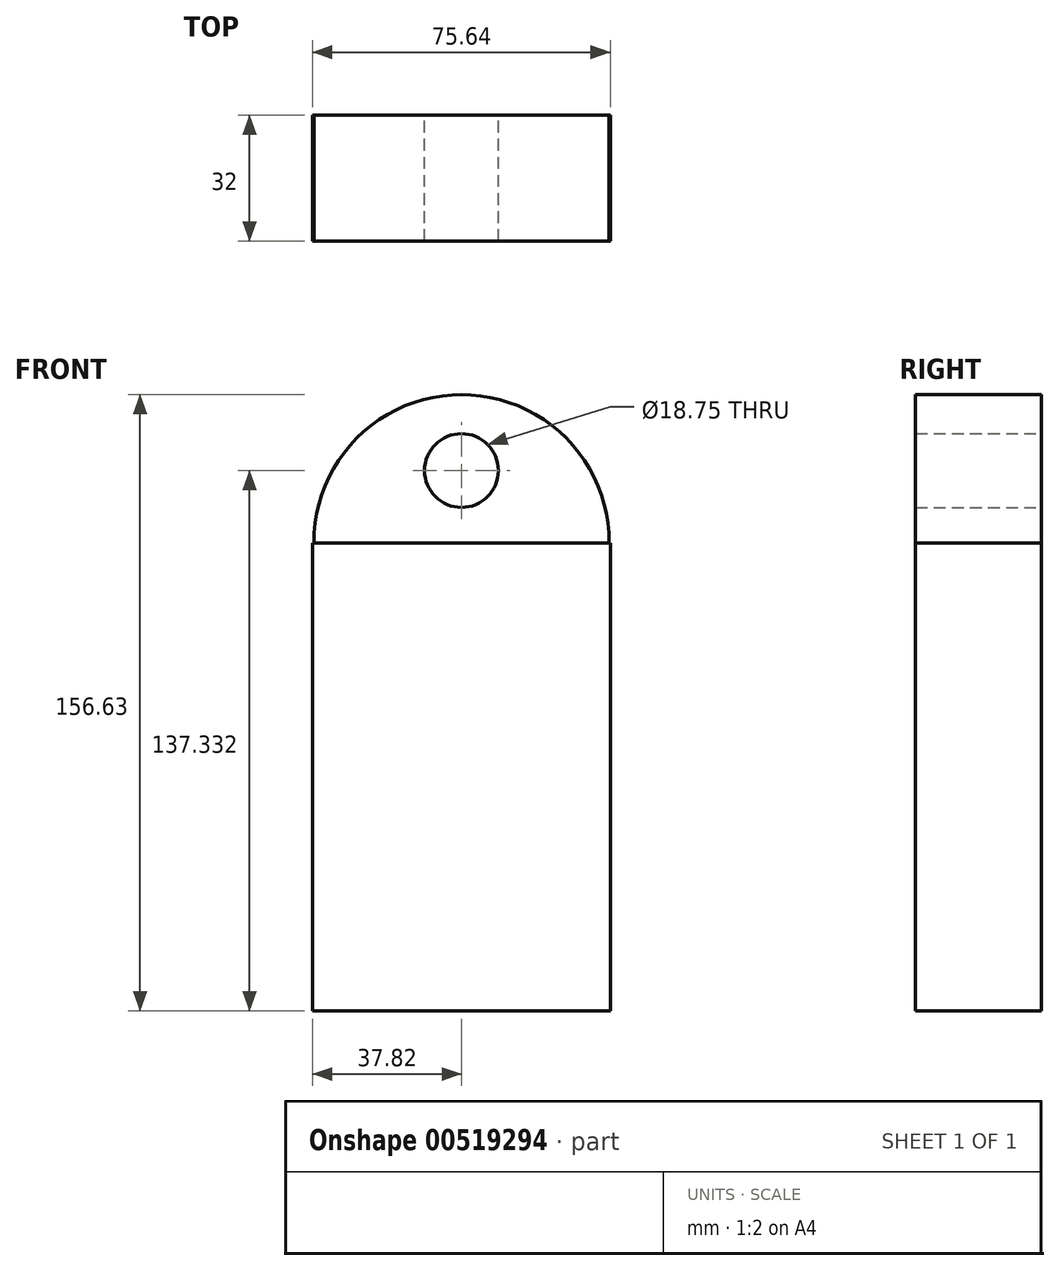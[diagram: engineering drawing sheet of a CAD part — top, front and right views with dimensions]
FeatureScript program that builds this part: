
annotation { "Feature Type Name" : "Feature", "Feature Type Description" : "" }
export const myFeature = defineFeature(function(context is Context, id is Id, definition is map)
    precondition{}
    {
        {
            var Q0;
            Q0=qCreatedBy(makeId("Front.planeOp"),FACE);
            var sketch = newSketch(context, id + "F0", { "sketchPlane" : qUnion([Q0])});
            skLineSegment(sketch, "E0.bottom", {"start": v(-37.82, 59.48) * mm, "end": v(37.82, 59.48) * mm});
            skLineSegment(sketch, "E0.top", {"start": v(-37.82, -59.48) * mm, "end": v(37.82, -59.48) * mm});
            skLineSegment(sketch, "E0.left", {"start": v(-37.82, 59.48) * mm, "end": v(-37.82, -59.48) * mm});
            skLineSegment(sketch, "E0.right", {"start": v(37.82, 59.48) * mm, "end": v(37.82, -59.48) * mm});
            skPoint(sketch, "E0.middle", {"position": v(0, 0) * mm});
            skSolve(sketch);
        }
        {
            var Q0;
            Q0=makeQuery(id+"F0.imprint","IMPRINT",FACE,{"disambiguationData":[TD([[makeQuery(id+"F0.imprint","IMPRINT",EDGE,{"derivedFrom":sQuery(id+"F0.wireOp",EDGE,"E0.bottom")}),-1.0]])]});
            var sketch = newSketch(context, id + "F1", { "sketchPlane" : qUnion([Q0])});
            skCircle(sketch, "E1", {"center": v(0, 59.66) * mm, "radius": 37.49 * mm});
            skSolve(sketch);
        }
        {
            var Q0;
            {var subQ0=sQuery(id+"F1.wireOp",EDGE,"E1");var subQ1=makeQuery(id+"F0.imprint","IMPRINT",EDGE,{"derivedFrom":sQuery(id+"F0.wireOp",EDGE,"E0.bottom")});var subQ2=makeQuery(id+"F1.imprint","INTERSECT",VERTEX,{"disambiguationData":[OD(0.0)],"derivedFrom":[subQ1,subQ0]});Q0=makeQuery(id+"F1.imprint","IMPRINT",FACE,{"disambiguationData":[TD([[makeQuery(id+"F1.imprint","IMPRINT",EDGE,{"disambiguationData":[TD([[subQ2,-1.0]])],"derivedFrom":subQ0}),1.0]])]});}
            var Q1;
            {var subQ0=sQuery(id+"F1.wireOp",EDGE,"E1");var subQ1=makeQuery(id+"F0.imprint","IMPRINT",EDGE,{"derivedFrom":sQuery(id+"F0.wireOp",EDGE,"E0.bottom")});var subQ2=makeQuery(id+"F1.imprint","INTERSECT",VERTEX,{"disambiguationData":[OD(0.0)],"derivedFrom":[subQ1,subQ0]});Q1=makeQuery(id+"F1.imprint","IMPRINT",FACE,{"disambiguationData":[TD([[makeQuery(id+"F1.imprint","IMPRINT",EDGE,{"disambiguationData":[TD([[subQ2,1.0]])],"derivedFrom":subQ0}),1.0]])]});}
            var Q2;
            Q2=makeQuery(id+"F0.imprint","IMPRINT",FACE,{"disambiguationData":[TD([[makeQuery(id+"F0.imprint","IMPRINT",EDGE,{"derivedFrom":sQuery(id+"F0.wireOp",EDGE,"E0.bottom")}),-1.0]])]});
            var Q3;
            Q3=makeQuery(id+"F1.imprint","IMPRINT",FACE,{"disambiguationData":[TD([[makeQuery(id+"F1.imprint","IMPRINT",EDGE,{"derivedFrom":makeQuery(id+"F0.imprint","IMPRINT",EDGE,{"derivedFrom":sQuery(id+"F0.wireOp",EDGE,"E0.top")})}),1.0]])]});
            extrude(context, id + "F2", {"entities" : qUnion([Q0, Q1, Q2, Q3]), "endBound" : BoundingType.SYMMETRIC, "depth" : 32 * mm, "offsetDistance" : 25.4 * mm});
        }
        {
            var Q0;
            Q0=makeQuery(id+"F2.opExtrude","CAP_FACE",FACE,{"disambiguationData":[OSD([sQuery(id+"F0.wireOp",EDGE,"E0.bottom"),sQuery(id+"F0.wireOp",EDGE,"E0.top"),sQuery(id+"F0.wireOp",EDGE,"E0.left"),sQuery(id+"F0.wireOp",EDGE,"E0.right"),sQuery(id+"F1.wireOp",EDGE,"E1")])],"isStart":true});
            var sketch = newSketch(context, id + "F3", { "sketchPlane" : qUnion([Q0])});
            skCircle(sketch, "E2", {"center": v(0, 77.85) * mm, "radius": 9.38 * mm});
            skCircle(sketch, "E3", {"center": v(0, 47.67) * mm, "radius": 9.38 * mm});
            skCircle(sketch, "E4", {"center": v(0, 26.83) * mm, "radius": 8.62 * mm});
            skCircle(sketch, "E5", {"center": v(0, -14.84) * mm, "radius": 9.36 * mm});
            skCircle(sketch, "E6", {"center": v(0, -42.87) * mm, "radius": 8.62 * mm});
            skSolve(sketch);
        }
        {
            var Q0;
            Q0=makeQuery(id+"F3.imprint","IMPRINT",FACE,{"disambiguationData":[TD([[makeQuery(id+"F3.imprint","IMPRINT",EDGE,{"derivedFrom":sQuery(id+"F3.wireOp",EDGE,"E2")}),1.0]])]});
            extrude(context, id + "F4", {"entities" : qUnion([Q0]), "operationType" : NewBodyOperationType.REMOVE, "oppositeDirection" : true, "depth" : 89.66 * mm, "offsetDistance" : 25.4 * mm});
        }
    });
